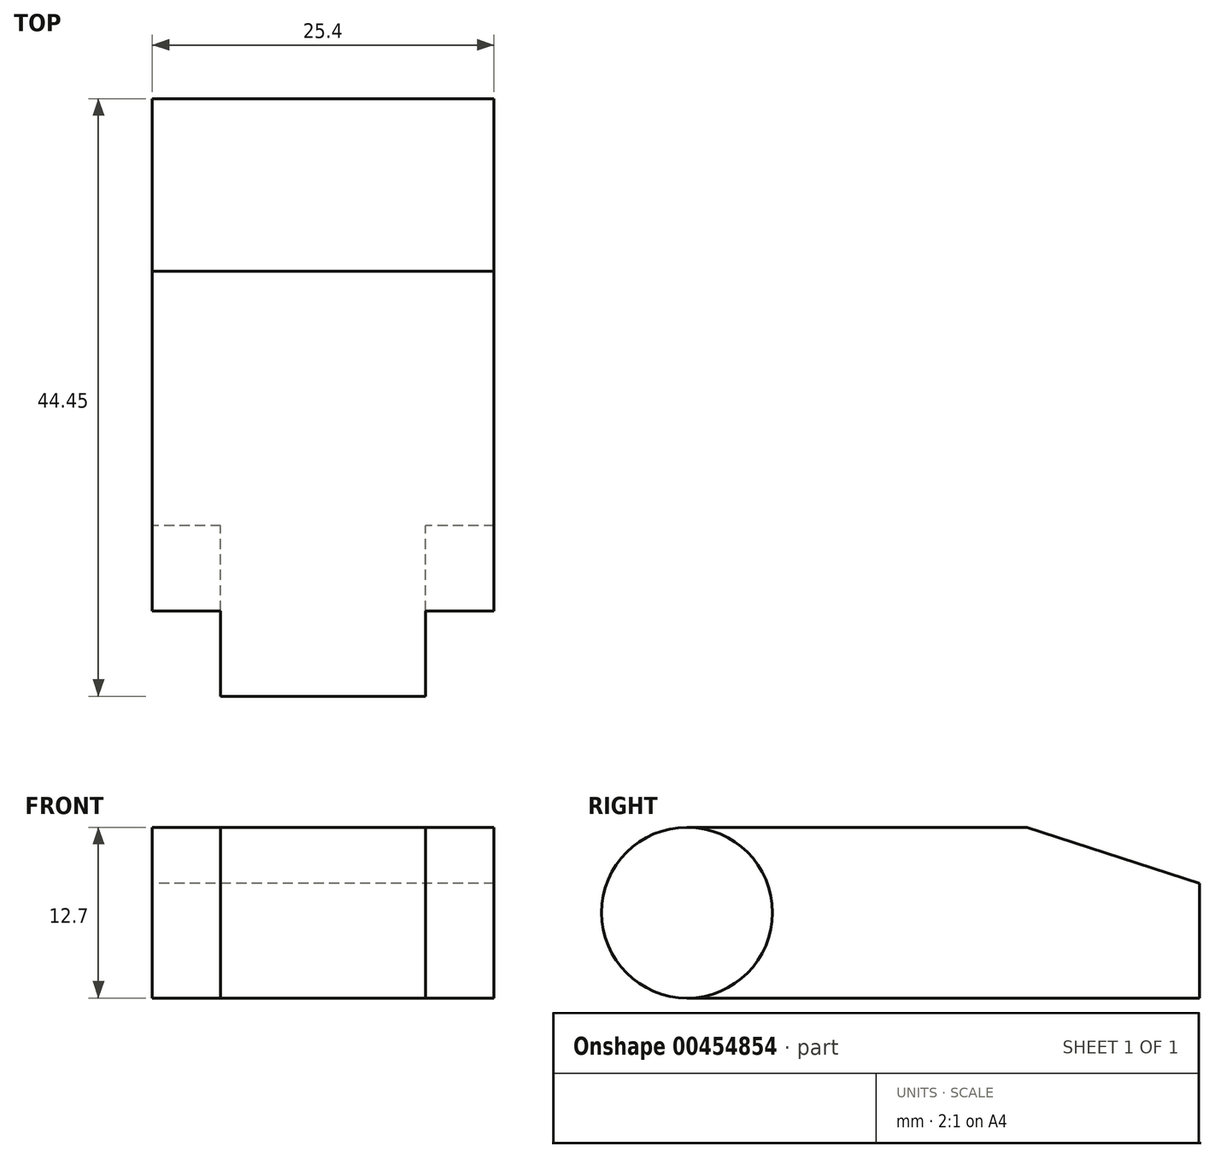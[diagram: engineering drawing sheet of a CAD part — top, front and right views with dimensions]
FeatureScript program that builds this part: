
annotation { "Feature Type Name" : "Feature", "Feature Type Description" : "" }
export const myFeature = defineFeature(function(context is Context, id is Id, definition is map)
    precondition{}
    {
        {
            var Q0;
            Q0=qCreatedBy(makeId("Right.planeOp"),FACE);
            var sketch = newSketch(context, id + "F0", { "sketchPlane" : qUnion([Q0])});
            skLineSegment(sketch, "E0.bottom", {"start": v(6.21, 6.35) * mm, "end": v(-19.05, 6.35) * mm});
            skLineSegment(sketch, "E0.top", {"start": v(10.47, -6.35) * mm, "end": v(-19.05, -6.35) * mm});
            skLineSegment(sketch, "E0.left", {"start": v(19.05, 2.2) * mm, "end": v(19.05, -6.35) * mm});
            skLineSegment(sketch, "E0.right", {"start": v(-19.05, 6.35) * mm, "end": v(-19.05, -6.35) * mm});
            skPoint(sketch, "E0.middle", {"position": v(0, 0) * mm});
            skCircle(sketch, "E1", {"center": v(-19.05, 0) * mm, "radius": 6.35 * mm});
            skLineSegment(sketch, "E2", {"start": v(10.47, -6.35) * mm, "end": v(19.05, -6.35) * mm});
            skLineSegment(sketch, "E3", {"start": v(6.21, 6.35) * mm, "end": v(19.05, 2.2) * mm});
            skPoint(sketch, "E4.start.orphan", {"position": v(19.05, 6.35) * mm});
            skSolve(sketch);
        }
        {
            var Q0;
            {var subQ0=sQuery(id+"F0.wireOp",EDGE,"E0.bottom");Q0=makeQuery(id+"F0.imprint","IMPRINT",FACE,{"disambiguationData":[TD([[makeQuery(id+"F0.imprint","IMPRINT",EDGE,{"derivedFrom":subQ0}),1.0]])]});}
            var Q1;
            Q1=makeQuery(id+"F0.imprint","IMPRINT",FACE,{"disambiguationData":[TD([[makeQuery(id+"F0.imprint","IMPRINT",EDGE,{"derivedFrom":sQuery(id+"F0.wireOp",EDGE,"E0.left")}),1.0]])]});
            extrude(context, id + "F1", {"entities" : qUnion([Q0, Q1]), "endBound" : BoundingType.SYMMETRIC, "depth" : 25.4 * mm, "offsetDistance" : 25.4 * mm});
        }
        {
            var Q0;
            {var subQ0=sQuery(id+"F0.wireOp",EDGE,"E0.right");Q0=makeQuery(id+"F0.imprint","IMPRINT",FACE,{"disambiguationData":[TD([[makeQuery(id+"F0.imprint","IMPRINT",EDGE,{"derivedFrom":subQ0}),1.0]])]});}
            var Q1;
            {var subQ0=sQuery(id+"F0.wireOp",EDGE,"E0.right");Q1=makeQuery(id+"F0.imprint","IMPRINT",FACE,{"disambiguationData":[TD([[makeQuery(id+"F0.imprint","IMPRINT",EDGE,{"derivedFrom":subQ0}),-1.0]])]});}
            extrude(context, id + "F2", {"entities" : qUnion([Q0, Q1]), "operationType" : NewBodyOperationType.ADD, "endBound" : BoundingType.SYMMETRIC, "depth" : 15.24 * mm, "offsetDistance" : 25.4 * mm});
        }
    });
